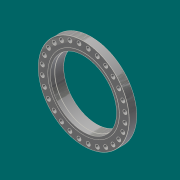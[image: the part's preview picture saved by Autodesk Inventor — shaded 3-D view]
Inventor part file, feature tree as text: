
AUTODESK INVENTOR PART (.ipt)
format: ipt  version: 2017.3 (Build 213257000, 257)  size: 376,832 bytes
history: native  units: in
note: dims shown in document units (in); Inventor stores cm internally (conversion verified against a paired STEP export)
features: sketch x5, extrude x3, chamfer x3, fillet x2, hole x1, pattern_circular x1, revolve x1
ambient origin geometry x8: Origin, YZ Plane, XZ Plane, XY Plane, X Axis, Y Axis, Z Axis, Center Point
bodies: Solid1 (feature_tree)
feature tree (16):
  extrude  "Extrusion1"  Depth=31.0in
  extrude  "Extrusion2"  Depth=3.625in
  extrude  "Extrusion3"  Depth=0.0625in
  hole  "Hole1"  [1 undecoded]
  chamfer  "Chamfer3"  Distance=11.0236in Angle=360.0deg
  pattern_circular  "Circular Pattern1"  [2 undecoded]
  chamfer  "Chamfer2"  Distance=0.4375in
  fillet  "Fillet2"  Radius=0.0312in
  chamfer  "Chamfer4"  Distance=0.0625in Angle=45.0deg
  revolve  "Revolution1"  Angle=90.0deg
  fillet  "Fillet5"  Radius=2.0in
  sketch  "Sketch1"  dims[d0=43.0in d1=31.0in]
  sketch  "Sketch2"  dims[d2=3.625in d3=0.0in d4=33.75in]
  sketch  "Sketch3"  dims[d5=0.0625in d6=0.0in d7=34.75in]
  sketch  "Sketch4"  dims[d8=2.4375in d9=0.0in d13=19.625in]
  sketch  "Sketch6"  dims[d14=0.0442in d15=1.875in d16=0.75in d17=0.375in d18=0.25in d19=0.5635in d20=1.0in d21=0.8108in d22=11.0236in d23=360.0deg d25=0.0625in d26=0.125in d27=0.0687in d29=0.4375in d30=0.0312in d31=0.125in d32=45.0deg d33=0.0625in d34=0.125in d35=45.0deg d49=90.0deg d71=2.0in d72=15.625in d73=0.0312in d94=16.0in d95=0.4375in d96=0.2577in d99=0.5in d100=0.625in d101=0.2893in]
note: 3 required parameter values undecoded (feature->parameter linkage not recoverable at this tier; creation-order binding heuristic only, values carry confidence <= 0.55)
